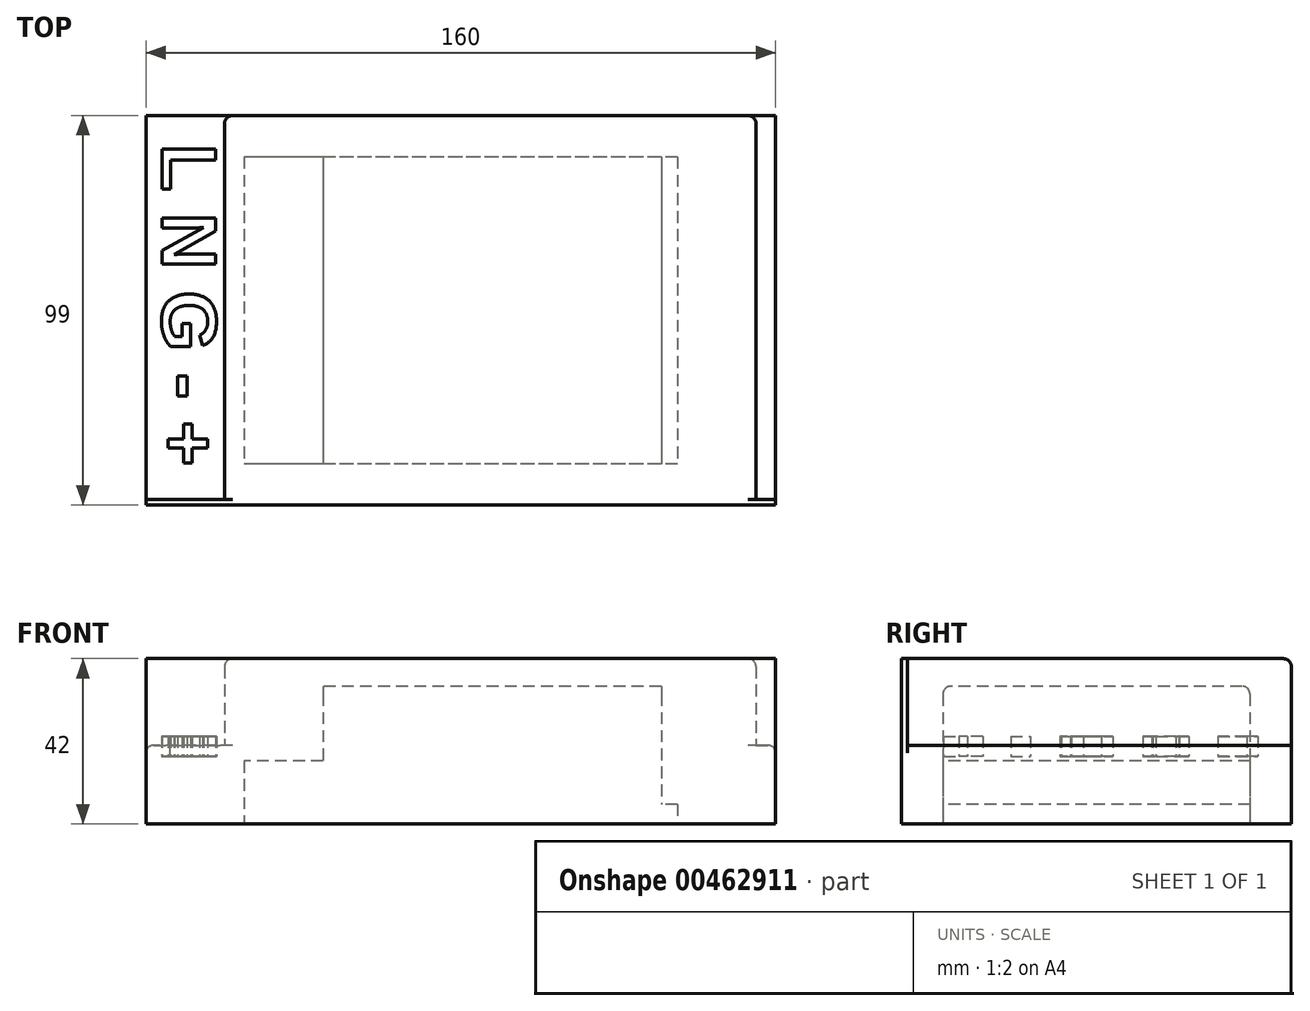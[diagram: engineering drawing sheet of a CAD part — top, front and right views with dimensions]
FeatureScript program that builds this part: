
annotation { "Feature Type Name" : "Feature", "Feature Type Description" : "" }
export const myFeature = defineFeature(function(context is Context, id is Id, definition is map)
    precondition{}
    {
        {
            var Q0;
            Q0=qCreatedBy(makeId("Top.planeOp"),FACE);
            var sketch = newSketch(context, id + "F0", { "sketchPlane" : qUnion([Q0])});
            skLineSegment(sketch, "E0.bottom", {"start": v(55, 39) * mm, "end": v(-55, 39) * mm});
            skLineSegment(sketch, "E0.top", {"start": v(55, -39) * mm, "end": v(-55, -39) * mm});
            skLineSegment(sketch, "E0.left", {"start": v(55, 39) * mm, "end": v(55, -39) * mm});
            skLineSegment(sketch, "E0.right", {"start": v(-55, 39) * mm, "end": v(-55, -39) * mm});
            skPoint(sketch, "E0.middle", {"position": v(0, 0) * mm});
            skLineSegment(sketch, "E1", {"start": v(-35, 39) * mm, "end": v(-35, -39) * mm});
            skLineSegment(sketch, "E2", {"start": v(51, 39) * mm, "end": v(51, -39) * mm});
            skLineSegment(sketch, "E3.bottom", {"start": v(80, 49.5) * mm, "end": v(-80, 49.5) * mm});
            skLineSegment(sketch, "E3.top", {"start": v(80, -49.5) * mm, "end": v(-80, -49.5) * mm});
            skLineSegment(sketch, "E3.left", {"start": v(80, 49.5) * mm, "end": v(80, -49.5) * mm});
            skLineSegment(sketch, "E3.right", {"start": v(-80, 49.5) * mm, "end": v(-80, -49.5) * mm});
            skLineSegment(sketch, "E4", {"start": v(-80, -48) * mm, "end": v(80, -48) * mm});
            skLineSegment(sketch, "E5", {"start": v(-60, 49.5) * mm, "end": v(-60, -48) * mm});
            skLineSegment(sketch, "E6", {"start": v(75, 49.5) * mm, "end": v(75, -48) * mm});
            skSolve(sketch);
        }
        {
            var Q0;
            {var subQ0=sQuery(id+"F0.wireOp",EDGE,"E1");Q0=makeQuery(id+"F0.imprint","IMPRINT",FACE,{"disambiguationData":[TD([[makeQuery(id+"F0.imprint","IMPRINT",EDGE,{"derivedFrom":subQ0}),1.0]])]});}
            extrude(context, id + "F1", {"entities" : qUnion([Q0]), "depth" : 35 * mm, "offsetDistance" : 25.4 * mm});
        }
        {
            var Q0;
            {var subQ0=sQuery(id+"F0.wireOp",EDGE,"E0.right");Q0=makeQuery(id+"F0.imprint","IMPRINT",FACE,{"disambiguationData":[TD([[makeQuery(id+"F0.imprint","IMPRINT",EDGE,{"derivedFrom":subQ0}),1.0]])]});}
            extrude(context, id + "F2", {"entities" : qUnion([Q0]), "operationType" : NewBodyOperationType.ADD, "depth" : 16 * mm, "offsetDistance" : 25.4 * mm});
        }
        {
            var Q0;
            {var subQ0=sQuery(id+"F0.wireOp",EDGE,"E0.left");Q0=makeQuery(id+"F0.imprint","IMPRINT",FACE,{"disambiguationData":[TD([[makeQuery(id+"F0.imprint","IMPRINT",EDGE,{"derivedFrom":subQ0}),-1.0]])]});}
            extrude(context, id + "F3", {"entities" : qUnion([Q0]), "operationType" : NewBodyOperationType.ADD, "depth" : 5 * mm, "offsetDistance" : 25.4 * mm});
        }
        {
            var Q0;
            Q0=makeQuery(id+"F1.opExtrude","CAP_EDGE",EDGE,{"disambiguationData":[OSD([sQuery(id+"F0.wireOp",EDGE,"E0.bottom")])],"isStart":false});
            var Q1;
            Q1=makeQuery(id+"F1.opExtrude","CAP_EDGE",EDGE,{"disambiguationData":[OSD([sQuery(id+"F0.wireOp",EDGE,"E0.top")])],"isStart":false});
            fillet(context, id + "F4", {"entities" : qUnion([Q0, Q1]), "radius" : 2 * mm, "tangentPropagation" : true, "allowEdgeOverflow" : false});
        }
        {
            var Q0;
            {var subQ1=sQuery(id+"F0.wireOp",EDGE,"E0.left");Q0=makeQuery(id+"F0.imprint","IMPRINT",FACE,{"disambiguationData":[TD([[makeQuery(id+"F0.imprint","IMPRINT",EDGE,{"derivedFrom":subQ1}),1.0]])]});}
            var Q1;
            {var subQ0=sQuery(id+"F0.wireOp",EDGE,"E0.right");Q1=makeQuery(id+"F0.imprint","IMPRINT",FACE,{"disambiguationData":[TD([[makeQuery(id+"F0.imprint","IMPRINT",EDGE,{"derivedFrom":subQ0}),1.0]])]});}
            var Q2;
            {var subQ0=sQuery(id+"F0.wireOp",EDGE,"E1");Q2=makeQuery(id+"F0.imprint","IMPRINT",FACE,{"disambiguationData":[TD([[makeQuery(id+"F0.imprint","IMPRINT",EDGE,{"derivedFrom":subQ0}),1.0]])]});}
            var Q3;
            {var subQ0=sQuery(id+"F0.wireOp",EDGE,"E0.left");Q3=makeQuery(id+"F0.imprint","IMPRINT",FACE,{"disambiguationData":[TD([[makeQuery(id+"F0.imprint","IMPRINT",EDGE,{"derivedFrom":subQ0}),-1.0]])]});}
            extrude(context, id + "F5", {"entities" : qUnion([Q0, Q1, Q2, Q3]), "depth" : 42 * mm, "offsetDistance" : 25.4 * mm});
        }
        {
            var Q0;
            {var subQ3=sQuery(id+"F0.wireOp",EDGE,"E6");Q0=makeQuery(id+"F0.imprint","IMPRINT",FACE,{"disambiguationData":[TD([[makeQuery(id+"F0.imprint","IMPRINT",EDGE,{"derivedFrom":subQ3}),1.0]])]});}
            extrude(context, id + "F6", {"entities" : qUnion([Q0]), "operationType" : NewBodyOperationType.ADD, "depth" : 20 * mm, "offsetDistance" : 25.4 * mm});
        }
        {
            var Q0;
            {var subQ3=sQuery(id+"F0.wireOp",EDGE,"E5");Q0=makeQuery(id+"F0.imprint","IMPRINT",FACE,{"disambiguationData":[TD([[makeQuery(id+"F0.imprint","IMPRINT",EDGE,{"derivedFrom":subQ3}),-1.0]])]});}
            extrude(context, id + "F7", {"entities" : qUnion([Q0]), "operationType" : NewBodyOperationType.ADD, "depth" : 20 * mm, "offsetDistance" : 25.4 * mm});
        }
        {
            var Q0;
            {var subQ1=sQuery(id+"F0.wireOp",EDGE,"E3.top");Q0=makeQuery(id+"F0.imprint","IMPRINT",FACE,{"disambiguationData":[TD([[makeQuery(id+"F0.imprint","IMPRINT",EDGE,{"derivedFrom":subQ1}),-1.0]])]});}
            extrude(context, id + "F8", {"entities" : qUnion([Q0]), "operationType" : NewBodyOperationType.ADD, "depth" : 42 * mm, "offsetDistance" : 25.4 * mm});
        }
        {
            var Q0;
            Q0=makeQuery(id+"F5.opExtrude","CAP_EDGE",EDGE,{"disambiguationData":[OSD([sQuery(id+"F0.wireOp",EDGE,"E3.bottom")])],"isStart":false});
            var Q1;
            Q1=makeQuery(id+"F7.opExtrude","CAP_EDGE",EDGE,{"disambiguationData":[OSD([sQuery(id+"F0.wireOp",EDGE,"E3.right")])],"isStart":false});
            var Q2;
            Q2=makeQuery(id+"F5.opExtrude","CAP_EDGE",EDGE,{"disambiguationData":[OSD([sQuery(id+"F0.wireOp",EDGE,"E5")])],"isStart":false});
            var Q3;
            Q3=makeQuery(id+"F5.opExtrude","CAP_EDGE",EDGE,{"disambiguationData":[OSD([sQuery(id+"F0.wireOp",EDGE,"E6")])],"isStart":false});
            var Q4;
            Q4=makeQuery(id+"F6.opExtrude","CAP_EDGE",EDGE,{"disambiguationData":[OSD([sQuery(id+"F0.wireOp",EDGE,"E3.left")])],"isStart":false});
            var Q5;
            Q5=makeQuery(id+"F5.opExtrude","SWEPT_EDGE",EDGE,{"disambiguationData":[OSD([sQuery(id+"F0.wireOp",EDGE,"E3.bottom"),sQuery(id+"F0.wireOp",EDGE,"E6")])]});
            var Q6;
            Q6=makeQuery(id+"F5.opExtrude","SWEPT_EDGE",EDGE,{"disambiguationData":[OSD([sQuery(id+"F0.wireOp",EDGE,"E3.bottom"),sQuery(id+"F0.wireOp",EDGE,"E5")])]});
            fillet(context, id + "F9", {"entities" : qUnion([Q0, Q1, Q2, Q3, Q4, Q5, Q6]), "radius" : 2 * mm, "tangentPropagation" : true, "allowEdgeOverflow" : false});
        }
        {
            var Q0;
            Q0=makeQuery(id+"F7.opExtrude","CAP_FACE",FACE,{"disambiguationData":[OSD([sQuery(id+"F0.wireOp",EDGE,"E3.bottom"),sQuery(id+"F0.wireOp",EDGE,"E3.right"),sQuery(id+"F0.wireOp",EDGE,"E4"),sQuery(id+"F0.wireOp",EDGE,"E5")])],"isStart":false});
            var sketch = newSketch(context, id + "F10", { "sketchPlane" : qUnion([Q0])});
            skText(sketch, "E7", { "text": "L N G - +", "fontName": "Arimo-Bold.ttf"});
            const initialGuessF10  = {"E7": [-0.07915, -0.0413, 1, 0, 0.01426]};
            skSetInitialGuess(sketch, initialGuessF10);
            skSolve(sketch);
        }
        {
            var Q0;
            Q0 = qSketchRegion(id + "F10", true);
            extrude(context, id + "F11", {"entities" : qUnion([Q0]), "depth" : 5.08 * mm, "offsetDistance" : 25.4 * mm});
        }
        {
            var Q0;
            Q0=makeQuery(id+"F11.opExtrude","SWEPT_BODY",BODY,{"disambiguationData":[OSD([sQuery(id+"F10.wireOp",EDGE,"E7.sketch_text.stroke-0"),sQuery(id+"F10.wireOp",EDGE,"E7.sketch_text.stroke-1"),sQuery(id+"F10.wireOp",EDGE,"E7.sketch_text.stroke-2"),sQuery(id+"F10.wireOp",EDGE,"E7.sketch_text.stroke-3"),sQuery(id+"F10.wireOp",EDGE,"E7.sketch_text.stroke-4"),sQuery(id+"F10.wireOp",EDGE,"E7.sketch_text.stroke-5")])]});
            var Q1;
            Q1=makeQuery(id+"F11.opExtrude","SWEPT_BODY",BODY,{"disambiguationData":[OSD([sQuery(id+"F10.wireOp",EDGE,"E7.sketch_text.stroke-6"),sQuery(id+"F10.wireOp",EDGE,"E7.sketch_text.stroke-7"),sQuery(id+"F10.wireOp",EDGE,"E7.sketch_text.stroke-8"),sQuery(id+"F10.wireOp",EDGE,"E7.sketch_text.stroke-9"),sQuery(id+"F10.wireOp",EDGE,"E7.sketch_text.stroke-10"),sQuery(id+"F10.wireOp",EDGE,"E7.sketch_text.stroke-11"),sQuery(id+"F10.wireOp",EDGE,"E7.sketch_text.stroke-12"),sQuery(id+"F10.wireOp",EDGE,"E7.sketch_text.stroke-13"),sQuery(id+"F10.wireOp",EDGE,"E7.sketch_text.stroke-14"),sQuery(id+"F10.wireOp",EDGE,"E7.sketch_text.stroke-15"),sQuery(id+"F10.wireOp",EDGE,"E7.sketch_text.stroke-16"),sQuery(id+"F10.wireOp",EDGE,"E7.sketch_text.stroke-17")])]});
            var Q2;
            Q2=makeQuery(id+"F11.opExtrude","SWEPT_BODY",BODY,{"disambiguationData":[OSD([sQuery(id+"F10.wireOp",EDGE,"E7.sketch_text.stroke-18"),sQuery(id+"F10.wireOp",EDGE,"E7.sketch_text.stroke-19"),sQuery(id+"F10.wireOp",EDGE,"E7.sketch_text.stroke-20"),sQuery(id+"F10.wireOp",EDGE,"E7.sketch_text.stroke-21"),sQuery(id+"F10.wireOp",EDGE,"E7.sketch_text.stroke-22"),sQuery(id+"F10.wireOp",EDGE,"E7.sketch_text.stroke-23"),sQuery(id+"F10.wireOp",EDGE,"E7.sketch_text.stroke-24"),sQuery(id+"F10.wireOp",EDGE,"E7.sketch_text.stroke-25"),sQuery(id+"F10.wireOp",EDGE,"E7.sketch_text.stroke-26"),sQuery(id+"F10.wireOp",EDGE,"E7.sketch_text.stroke-27"),sQuery(id+"F10.wireOp",EDGE,"E7.sketch_text.stroke-28"),sQuery(id+"F10.wireOp",EDGE,"E7.sketch_text.stroke-29"),sQuery(id+"F10.wireOp",EDGE,"E7.sketch_text.stroke-30"),sQuery(id+"F10.wireOp",EDGE,"E7.sketch_text.stroke-31"),sQuery(id+"F10.wireOp",EDGE,"E7.sketch_text.stroke-32"),sQuery(id+"F10.wireOp",EDGE,"E7.sketch_text.stroke-33"),sQuery(id+"F10.wireOp",EDGE,"E7.sketch_text.stroke-34"),sQuery(id+"F10.wireOp",EDGE,"E7.sketch_text.stroke-35"),sQuery(id+"F10.wireOp",EDGE,"E7.sketch_text.stroke-36"),sQuery(id+"F10.wireOp",EDGE,"E7.sketch_text.stroke-37"),sQuery(id+"F10.wireOp",EDGE,"E7.sketch_text.stroke-38")])]});
            var Q3;
            Q3=makeQuery(id+"F11.opExtrude","SWEPT_BODY",BODY,{"disambiguationData":[OSD([sQuery(id+"F10.wireOp",EDGE,"E7.sketch_text.stroke-39"),sQuery(id+"F10.wireOp",EDGE,"E7.sketch_text.stroke-40"),sQuery(id+"F10.wireOp",EDGE,"E7.sketch_text.stroke-41"),sQuery(id+"F10.wireOp",EDGE,"E7.sketch_text.stroke-42")])]});
            var Q4;
            Q4=makeQuery(id+"F11.opExtrude","SWEPT_BODY",BODY,{"disambiguationData":[OSD([sQuery(id+"F10.wireOp",EDGE,"E7.sketch_text.stroke-43"),sQuery(id+"F10.wireOp",EDGE,"E7.sketch_text.stroke-44"),sQuery(id+"F10.wireOp",EDGE,"E7.sketch_text.stroke-45"),sQuery(id+"F10.wireOp",EDGE,"E7.sketch_text.stroke-46"),sQuery(id+"F10.wireOp",EDGE,"E7.sketch_text.stroke-47"),sQuery(id+"F10.wireOp",EDGE,"E7.sketch_text.stroke-48"),sQuery(id+"F10.wireOp",EDGE,"E7.sketch_text.stroke-49"),sQuery(id+"F10.wireOp",EDGE,"E7.sketch_text.stroke-50"),sQuery(id+"F10.wireOp",EDGE,"E7.sketch_text.stroke-51"),sQuery(id+"F10.wireOp",EDGE,"E7.sketch_text.stroke-52"),sQuery(id+"F10.wireOp",EDGE,"E7.sketch_text.stroke-53"),sQuery(id+"F10.wireOp",EDGE,"E7.sketch_text.stroke-54")])]});
            var Q5;
            Q5=makeQuery(id+"F8.opExtrude","SWEPT_EDGE",EDGE,{"disambiguationData":[OSD([sQuery(id+"F0.wireOp",EDGE,"E3.top"),sQuery(id+"F0.wireOp",EDGE,"E3.right")])]});
            transform(context, id + "F12", {"entities" : qUnion([Q0, Q1, Q2, Q3, Q4]), "transformType" : TransformType.ROTATION, "transformAxis" : qUnion([Q5]), "angle" : 90 * degree, "makeCopy" : false});
        }
        {
            var Q0;
            Q0=makeQuery(id+"F11.opExtrude","SWEPT_BODY",BODY,{"disambiguationData":[OSD([sQuery(id+"F10.wireOp",EDGE,"E7.sketch_text.stroke-18"),sQuery(id+"F10.wireOp",EDGE,"E7.sketch_text.stroke-19"),sQuery(id+"F10.wireOp",EDGE,"E7.sketch_text.stroke-20"),sQuery(id+"F10.wireOp",EDGE,"E7.sketch_text.stroke-21"),sQuery(id+"F10.wireOp",EDGE,"E7.sketch_text.stroke-22"),sQuery(id+"F10.wireOp",EDGE,"E7.sketch_text.stroke-23"),sQuery(id+"F10.wireOp",EDGE,"E7.sketch_text.stroke-24"),sQuery(id+"F10.wireOp",EDGE,"E7.sketch_text.stroke-25"),sQuery(id+"F10.wireOp",EDGE,"E7.sketch_text.stroke-26"),sQuery(id+"F10.wireOp",EDGE,"E7.sketch_text.stroke-27"),sQuery(id+"F10.wireOp",EDGE,"E7.sketch_text.stroke-28"),sQuery(id+"F10.wireOp",EDGE,"E7.sketch_text.stroke-29"),sQuery(id+"F10.wireOp",EDGE,"E7.sketch_text.stroke-30"),sQuery(id+"F10.wireOp",EDGE,"E7.sketch_text.stroke-31"),sQuery(id+"F10.wireOp",EDGE,"E7.sketch_text.stroke-32"),sQuery(id+"F10.wireOp",EDGE,"E7.sketch_text.stroke-33"),sQuery(id+"F10.wireOp",EDGE,"E7.sketch_text.stroke-34"),sQuery(id+"F10.wireOp",EDGE,"E7.sketch_text.stroke-35"),sQuery(id+"F10.wireOp",EDGE,"E7.sketch_text.stroke-36"),sQuery(id+"F10.wireOp",EDGE,"E7.sketch_text.stroke-37"),sQuery(id+"F10.wireOp",EDGE,"E7.sketch_text.stroke-38")])]});
            var Q1;
            Q1=makeQuery(id+"F11.opExtrude","SWEPT_BODY",BODY,{"disambiguationData":[OSD([sQuery(id+"F10.wireOp",EDGE,"E7.sketch_text.stroke-6"),sQuery(id+"F10.wireOp",EDGE,"E7.sketch_text.stroke-7"),sQuery(id+"F10.wireOp",EDGE,"E7.sketch_text.stroke-8"),sQuery(id+"F10.wireOp",EDGE,"E7.sketch_text.stroke-9"),sQuery(id+"F10.wireOp",EDGE,"E7.sketch_text.stroke-10"),sQuery(id+"F10.wireOp",EDGE,"E7.sketch_text.stroke-11"),sQuery(id+"F10.wireOp",EDGE,"E7.sketch_text.stroke-12"),sQuery(id+"F10.wireOp",EDGE,"E7.sketch_text.stroke-13"),sQuery(id+"F10.wireOp",EDGE,"E7.sketch_text.stroke-14"),sQuery(id+"F10.wireOp",EDGE,"E7.sketch_text.stroke-15"),sQuery(id+"F10.wireOp",EDGE,"E7.sketch_text.stroke-16"),sQuery(id+"F10.wireOp",EDGE,"E7.sketch_text.stroke-17")])]});
            var Q2;
            Q2=makeQuery(id+"F11.opExtrude","SWEPT_BODY",BODY,{"disambiguationData":[OSD([sQuery(id+"F10.wireOp",EDGE,"E7.sketch_text.stroke-39"),sQuery(id+"F10.wireOp",EDGE,"E7.sketch_text.stroke-40"),sQuery(id+"F10.wireOp",EDGE,"E7.sketch_text.stroke-41"),sQuery(id+"F10.wireOp",EDGE,"E7.sketch_text.stroke-42")])]});
            var Q3;
            Q3=makeQuery(id+"F11.opExtrude","SWEPT_BODY",BODY,{"disambiguationData":[OSD([sQuery(id+"F10.wireOp",EDGE,"E7.sketch_text.stroke-43"),sQuery(id+"F10.wireOp",EDGE,"E7.sketch_text.stroke-44"),sQuery(id+"F10.wireOp",EDGE,"E7.sketch_text.stroke-45"),sQuery(id+"F10.wireOp",EDGE,"E7.sketch_text.stroke-46"),sQuery(id+"F10.wireOp",EDGE,"E7.sketch_text.stroke-47"),sQuery(id+"F10.wireOp",EDGE,"E7.sketch_text.stroke-48"),sQuery(id+"F10.wireOp",EDGE,"E7.sketch_text.stroke-49"),sQuery(id+"F10.wireOp",EDGE,"E7.sketch_text.stroke-50"),sQuery(id+"F10.wireOp",EDGE,"E7.sketch_text.stroke-51"),sQuery(id+"F10.wireOp",EDGE,"E7.sketch_text.stroke-52"),sQuery(id+"F10.wireOp",EDGE,"E7.sketch_text.stroke-53"),sQuery(id+"F10.wireOp",EDGE,"E7.sketch_text.stroke-54")])]});
            var Q4;
            Q4=makeQuery(id+"F11.opExtrude","SWEPT_BODY",BODY,{"disambiguationData":[OSD([sQuery(id+"F10.wireOp",EDGE,"E7.sketch_text.stroke-0"),sQuery(id+"F10.wireOp",EDGE,"E7.sketch_text.stroke-1"),sQuery(id+"F10.wireOp",EDGE,"E7.sketch_text.stroke-2"),sQuery(id+"F10.wireOp",EDGE,"E7.sketch_text.stroke-3"),sQuery(id+"F10.wireOp",EDGE,"E7.sketch_text.stroke-4"),sQuery(id+"F10.wireOp",EDGE,"E7.sketch_text.stroke-5")])]});
            transform(context, id + "F13", {"entities" : qUnion([Q0, Q1, Q2, Q3, Q4]), "transformType" : TransformType.TRANSLATION_3D, "dx" : -4.06 * mm, "dy" : 92.7 * mm, "dz" : -2.8 * mm, "makeCopy" : false});
        }
    });
